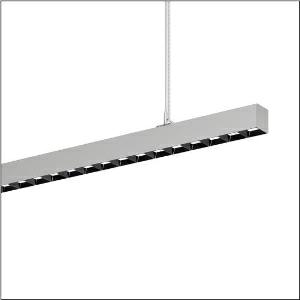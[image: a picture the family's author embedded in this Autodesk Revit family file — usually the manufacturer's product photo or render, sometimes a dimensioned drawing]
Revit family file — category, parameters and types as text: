
# Revit family: silica_r__21_51mx32dc4dsb_d767
name_source: partatom
category: Lighting Fixtures
units: mm (PartAtom-declared; Revit-internal decimal feet)

## family parameters
Cut with Voids When Loaded = No
Host = Face
Light Source = No
Part Type = Normal
Room Calculation Point = No
Round Connector Dimension = Use Diameter
Shared = No

## types (1)
- --- (1 x LED, 18230 lm, 105.8 W, 4000K)
    Apparent Load = 106 VA
    CIE Flux Codes = 86 99 100 59 100
    Color Rendering = 80
    Color Temperature = 4000K
    Default Elevation = 1800 mm
    Description = Silica® 21, office luminaire, primary light control with darklight reflector, of PMMA, black, CAT 2 (L<= 3000cd/m²), light emission: direct/indirect distribution, primary light characteristic: symmetric, installation type: suspended mounting, LED, rated luminous flux: 18.230lm, luminous efficacy: 172lm/W, light colour: 840, colour temperature: 4000K, with terminal, 3+2-pole, max. 2.5mm², mains connection: 220..240V, AC, 50/60Hz, rated input power: 105.8W, luminaire housing, of aluminium, metallic grey (RAL 9006), length: 3.004mm, width: 53mm, height: 53mm, protection rating (complete): IP20, insulation class (complete): insulation class I (protective earthing), certification: CE, permissible operating ambient temperature: 0..+35°C, standard: EN 50419, packaging unit: 1 piece
    Height = 53 mm
    Lamp = 1 x LED
    Lamp Light Flux = 18230 lm
    Lamp Power = 105.8 W
    Lamp count = 1
    Length = 3004 mm
    Luminous efficacy = 172 lm/W
    Manufacturer = Siteco
    ModVariant = No
    Model = 51MX32DC4DSB
    Mounting Place = Ceiling
    Mounting Type = Pendant
    Number of Poles = 1
    OnlyDefault = Yes
    Power Factor = 1
    Product Name = Silica® 21
    Product group = office luminaire | ceiling pendant
    ProductGroupID = 902
    Protection Class = Protection class I
    Protection Degree = IP 20
    RLX_Detail_Level = 1
    RLX_Emergency_Light_Flux = 0 lm
    RLX_Emergency_Type = 0
    RLX_Emergency_Type_DB = No
    RlxData = <blob elided: 64637 chars, md5=b920881d>
    Socket = socket
    Standby Power = 0 W
    System Light Flux = 18230 lm
    System Power = 106 W
    Type Comments = factory setting: luminous flux: 100 % | dim-lin: 254 | 366 mA
    Type Image = l_1313642.jpg
    URL = http://relux.com
    VarID = @adj_070837
    Voltage = 0 V
    Weight = 0.00 kg
    Width = 53 mm

## geometry (parser evidence)
native form markers: Blend x4, Sweep x12
no freeform markers — native parametric forms only
